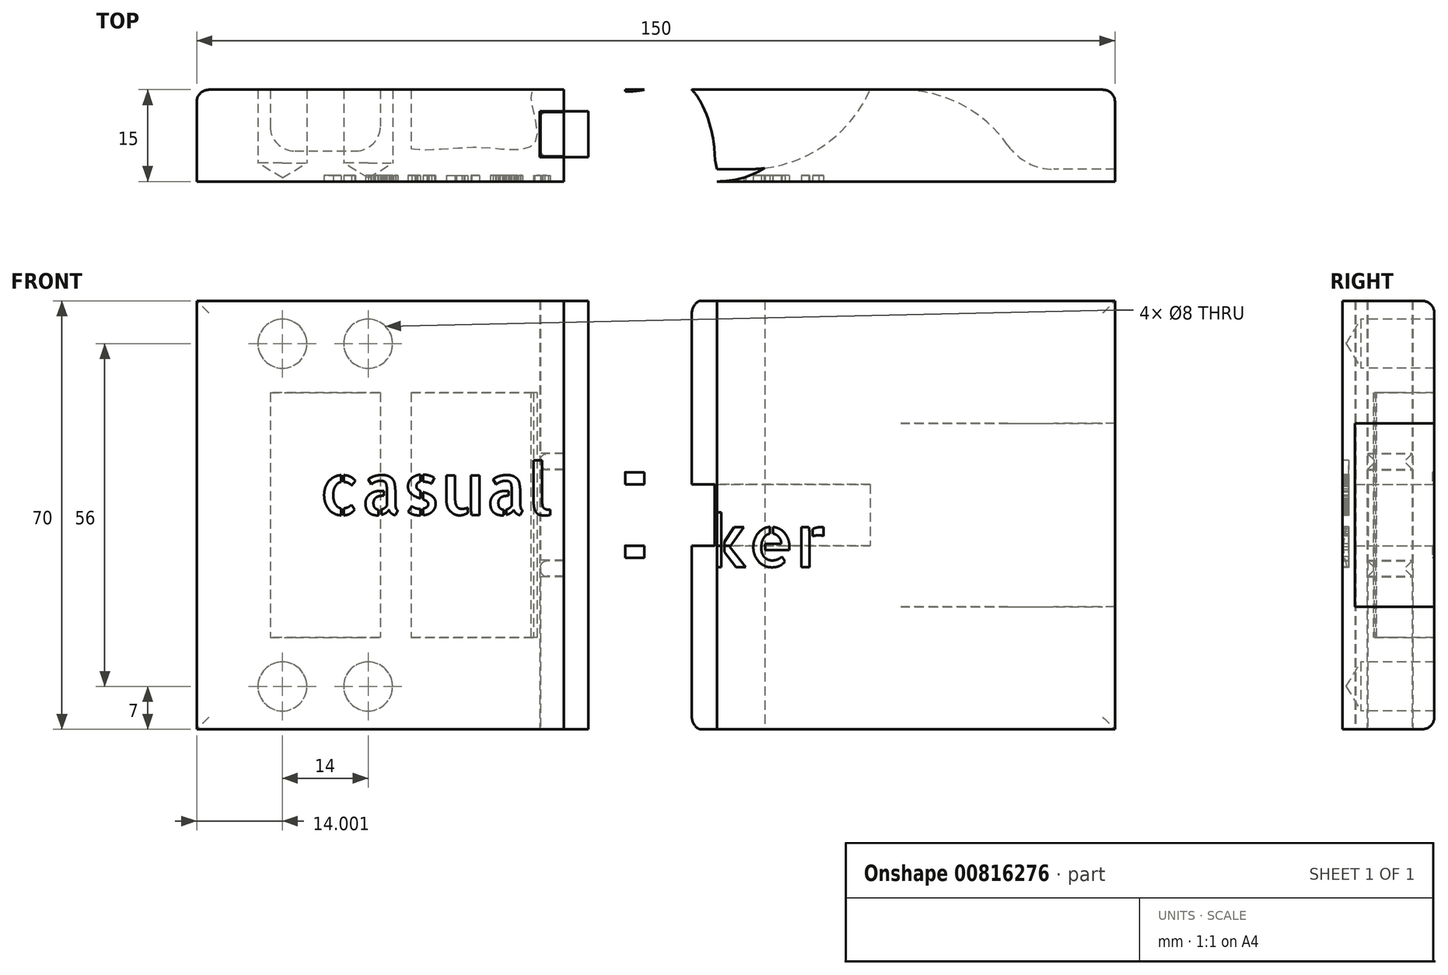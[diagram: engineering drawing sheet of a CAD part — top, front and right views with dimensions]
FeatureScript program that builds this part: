
annotation { "Feature Type Name" : "Feature", "Feature Type Description" : "" }
export const myFeature = defineFeature(function(context is Context, id is Id, definition is map)
    precondition{}
    {
        {
            var Q0;
            Q0=qCreatedBy(makeId("Top.planeOp"),FACE);
            var sketch = newSketch(context, id + "F0", { "sketchPlane" : qUnion([Q0])});
            skLineSegment(sketch, "E0.bottom", {"start": v(91.44, -7.74) * mm, "end": v(-58.56, -7.74) * mm});
            skLineSegment(sketch, "E0.top", {"start": v(91.44, 7.26) * mm, "end": v(-58.56, 7.26) * mm});
            skLineSegment(sketch, "E0.left", {"start": v(91.44, -7.74) * mm, "end": v(91.44, 7.26) * mm});
            skLineSegment(sketch, "E0.right", {"start": v(-58.56, -7.74) * mm, "end": v(-58.56, 7.26) * mm});
            skLineSegment(sketch, "E1", {"start": v(91.44, -5.74) * mm, "end": v(81.44, -5.74) * mm});
            skArc(sketch, "E2", {"start": v(81.44, -5.74) * mm, "mid": v(77.21, -4.7) * mm, "end": v(73.94, -1.84) * mm});
            skArc(sketch, "E3", {"start": v(73.94, -1.84) * mm, "mid": v(66.3, 4.85) * mm, "end": v(56.44, 7.26) * mm});
            skLineSegment(sketch, "E4", {"start": v(26.44, -5.74) * mm, "end": v(31.44, -5.74) * mm});
            skArc(sketch, "E5", {"start": v(31.44, -5.74) * mm, "mid": v(43.37, -2.2) * mm, "end": v(51.44, 7.26) * mm});
            skLineSegment(sketch, "E6", {"start": v(-58.56, -5.74) * mm, "end": v(106.76, -5.74) * mm, "construction": true});
            skFitSpline(sketch, "E7", {"points": [v(26.44, -5.74) * mm, v(25.26, -0.18) * mm, v(21.4, 5.71) * mm, v(6.44, 7.26) * mm], "startDerivative": vector(-4.01, 21.25) * mm, "endDerivative": vector(-55.89, 0) * mm});
            skLineSegment(sketch, "E8.bottom", {"start": v(-46.56, 7.26) * mm, "end": v(-28.56, 7.26) * mm});
            skLineSegment(sketch, "E8.top", {"start": v(-42.56, -2.74) * mm, "end": v(-32.56, -2.74) * mm});
            skLineSegment(sketch, "E8.left", {"start": v(-46.56, 7.26) * mm, "end": v(-46.56, 1.26) * mm});
            skLineSegment(sketch, "E8.right", {"start": v(-28.56, 7.26) * mm, "end": v(-28.56, 1.26) * mm});
            skLineSegment(sketch, "E9", {"start": v(-23.56, 7.26) * mm, "end": v(-23.56, -2.34) * mm});
            skFitSpline(sketch, "E10", {"points": [v(-23.56, -2.34) * mm, v(-16.77, -2.34) * mm, v(-10.45, -2.1) * mm, v(-4.83, 0) * mm, v(-3.56, 7.26) * mm], "startDerivative": vector(19.96, -2.18) * mm, "endDerivative": vector(3.98, 19.09) * mm});
            skPoint(sketch, "E11.visualSharp", {"position": v(-46.56, -2.74) * mm});
            skArc(sketch, "E11.filletArc", {"start": v(-46.56, 1.26) * mm, "mid": v(-45.39, -1.56) * mm, "end": v(-42.56, -2.74) * mm});
            skPoint(sketch, "E12.visualSharp", {"position": v(-28.56, -2.74) * mm});
            skArc(sketch, "E12.filletArc", {"start": v(-32.56, -2.74) * mm, "mid": v(-29.73, -1.56) * mm, "end": v(-28.56, 1.26) * mm});
            skCircle(sketch, "E13", {"center": v(26.44, 7.26) * mm, "radius": 15 * mm});
            skSolve(sketch);
        }
        {
            var Q0;
            Q0=qCreatedBy(makeId("Top.planeOp"),FACE);
            var sketch = newSketch(context, id + "F1", { "sketchPlane" : qUnion([Q0])});
            skFitSpline(sketch, "E14.0", {"points": [v(-23.56, -2.34) * mm, v(-21.87, -2.52) * mm, v(-16.45, -2.3) * mm, v(-10.78, -2.22) * mm, v(-3.3, -1.43) * mm, v(-3.9, 5.58) * mm, v(-3.56, 7.26) * mm]});
            skLineSegment(sketch, "E14.1", {"start": v(-23.56, 7.26) * mm, "end": v(-23.56, -2.34) * mm});
            skLineSegment(sketch, "E14.2", {"start": v(-28.56, 7.26) * mm, "end": v(-28.56, 1.26) * mm});
            skArc(sketch, "E14.3", {"start": v(-32.56, -2.74) * mm, "mid": v(-29.73, -1.56) * mm, "end": v(-28.56, 1.26) * mm});
            skLineSegment(sketch, "E14.4", {"start": v(-42.56, -2.74) * mm, "end": v(-32.56, -2.74) * mm});
            skArc(sketch, "E14.5", {"start": v(-46.56, 1.26) * mm, "mid": v(-45.39, -1.56) * mm, "end": v(-42.56, -2.74) * mm});
            skLineSegment(sketch, "E14.6", {"start": v(-46.56, 7.26) * mm, "end": v(-46.56, 1.26) * mm});
            skLineSegment(sketch, "E14.8", {"start": v(-58.56, -7.74) * mm, "end": v(-58.56, 7.26) * mm});
            skLineSegment(sketch, "E15", {"start": v(-58.56, -7.74) * mm, "end": v(1.44, -7.74) * mm});
            skLineSegment(sketch, "E16", {"start": v(1.44, -7.74) * mm, "end": v(1.44, 7.26) * mm});
            skLineSegment(sketch, "E17", {"start": v(1.44, 7.26) * mm, "end": v(-58.56, 7.26) * mm});
            skLineSegment(sketch, "E18.bottom", {"start": v(5.44, -3.75) * mm, "end": v(-2.56, -3.75) * mm});
            skLineSegment(sketch, "E18.top", {"start": v(5.44, 3.75) * mm, "end": v(-2.56, 3.75) * mm});
            skLineSegment(sketch, "E18.left", {"start": v(5.44, -3.75) * mm, "end": v(5.44, 3.75) * mm});
            skLineSegment(sketch, "E18.right", {"start": v(-2.56, -3.75) * mm, "end": v(-2.56, 3.75) * mm});
            skPoint(sketch, "E18.middle", {"position": v(1.44, 0) * mm});
            skFitSpline(sketch, "E19.0", {"points": [v(26.44, -5.74) * mm, v(26.08, -3.84) * mm, v(25.69, -0.2) * mm, v(21.45, 7.91) * mm, v(14.55, 7.26) * mm, v(6.44, 7.26) * mm]});
            skArc(sketch, "E19.1", {"start": v(31.44, -5.74) * mm, "mid": v(43.37, -2.2) * mm, "end": v(51.44, 7.26) * mm});
            skLineSegment(sketch, "E19.2", {"start": v(26.44, -5.74) * mm, "end": v(31.44, -5.74) * mm});
            skArc(sketch, "E19.3", {"start": v(73.94, -1.84) * mm, "mid": v(66.3, 4.85) * mm, "end": v(56.44, 7.26) * mm});
            skArc(sketch, "E19.4", {"start": v(81.44, -5.74) * mm, "mid": v(77.21, -4.7) * mm, "end": v(73.94, -1.84) * mm});
            skLineSegment(sketch, "E19.5", {"start": v(91.44, -5.74) * mm, "end": v(81.44, -5.74) * mm});
            skCircle(sketch, "E19.7", {"center": v(26.44, 7.26) * mm, "radius": 15 * mm});
            skLineSegment(sketch, "E20.bottom", {"start": v(1.44, 7.26) * mm, "end": v(91.44, 7.26) * mm});
            skLineSegment(sketch, "E20.top", {"start": v(1.44, -7.74) * mm, "end": v(91.44, -7.74) * mm});
            skLineSegment(sketch, "E20.left", {"start": v(1.44, 7.26) * mm, "end": v(1.44, -7.74) * mm});
            skLineSegment(sketch, "E20.right", {"start": v(91.44, 7.26) * mm, "end": v(91.44, -7.74) * mm});
            skLineSegment(sketch, "E21.0", {"start": v(8.94, 3.6) * mm, "end": v(-2.4, 3.6) * mm});
            skLineSegment(sketch, "E21.1", {"start": v(-2.4, -3.6) * mm, "end": v(-2.4, 3.6) * mm});
            skLineSegment(sketch, "E21.2", {"start": v(12.44, -3.6) * mm, "end": v(-2.4, -3.6) * mm});
            skSolve(sketch);
        }
        {
            var Q0;
            {var subQ5=sQuery(id+"F1.wireOp",EDGE,"E18.right");Q0=makeQuery(id+"F1.imprint","IMPRINT",FACE,{"disambiguationData":[TD([[makeQuery(id+"F1.imprint","IMPRINT",EDGE,{"derivedFrom":subQ5}),-1.0]])]});}
            var Q1;
            {var subQ6=sQuery(id+"F1.wireOp",EDGE,"E14.0");Q1=makeQuery(id+"F1.imprint","IMPRINT",FACE,{"disambiguationData":[TD([[makeQuery(id+"F1.imprint","IMPRINT",EDGE,{"derivedFrom":subQ6}),-1.0]])]});}
            var Q2;
            {var subQ0=sQuery(id+"F1.wireOp",EDGE,"E14.0");Q2=makeQuery(id+"F1.imprint","IMPRINT",FACE,{"disambiguationData":[TD([[makeQuery(id+"F1.imprint","IMPRINT",EDGE,{"derivedFrom":subQ0}),1.0]])]});}
            var Q3;
            {var subQ1=sQuery(id+"F1.wireOp",EDGE,"E14.2");Q3=makeQuery(id+"F1.imprint","IMPRINT",FACE,{"disambiguationData":[TD([[makeQuery(id+"F1.imprint","IMPRINT",EDGE,{"derivedFrom":subQ1}),-1.0]])]});}
            var Q4;
            {var subQ5=sQuery(id+"F1.wireOp",EDGE,"E21.1");Q4=makeQuery(id+"F1.imprint","IMPRINT",FACE,{"disambiguationData":[TD([[makeQuery(id+"F1.imprint","IMPRINT",EDGE,{"derivedFrom":subQ5}),-1.0]])]});}
            var Q5;
            {var subQ1=sQuery(id+"F1.wireOp",EDGE,"E14.1");Q5=makeQuery(id+"F1.imprint","IMPRINT",FACE,{"disambiguationData":[TD([[makeQuery(id+"F1.imprint","IMPRINT",EDGE,{"derivedFrom":subQ1}),-1.0]])]});}
            var Q6;
            {var subQ1=sQuery(id+"F1.wireOp",EDGE,"E21.1");var subQ3=sQuery(id+"F1.wireOp",EDGE,"E14.0");var subQ4=makeQuery(id+"F1.imprint","INTERSECT",VERTEX,{"derivedFrom":[subQ3,subQ1]});Q6=makeQuery(id+"F1.imprint","IMPRINT",FACE,{"disambiguationData":[TD([[makeQuery(id+"F1.imprint","IMPRINT",EDGE,{"disambiguationData":[TD([[subQ4,-1.0]])],"derivedFrom":subQ3}),-1.0]])]});}
            extrude(context, id + "F2", {"entities" : qUnion([Q0, Q1, Q2, Q3, Q4, Q5, Q6]), "depth" : 70 * mm, "offsetDistance" : 25 * mm, "symmetric" : true});
        }
        {
            var Q0;
            {var subQ1=sQuery(id+"F1.wireOp",EDGE,"E14.2");Q0=makeQuery(id+"F1.imprint","IMPRINT",FACE,{"disambiguationData":[TD([[makeQuery(id+"F1.imprint","IMPRINT",EDGE,{"derivedFrom":subQ1}),-1.0]])]});}
            var Q1;
            {var subQ0=sQuery(id+"F1.wireOp",EDGE,"E14.0");Q1=makeQuery(id+"F1.imprint","IMPRINT",FACE,{"disambiguationData":[TD([[makeQuery(id+"F1.imprint","IMPRINT",EDGE,{"derivedFrom":subQ0}),1.0]])]});}
            extrude(context, id + "F3", {"entities" : qUnion([Q0, Q1]), "operationType" : NewBodyOperationType.REMOVE, "depth" : 40 * mm, "offsetDistance" : 25 * mm, "symmetric" : true});
        }
        {
            var Q0;
            {var subQ5=sQuery(id+"F1.wireOp",EDGE,"E18.right");Q0=makeQuery(id+"F1.imprint","IMPRINT",FACE,{"disambiguationData":[TD([[makeQuery(id+"F1.imprint","IMPRINT",EDGE,{"derivedFrom":subQ5}),-1.0]])]});}
            var Q1;
            {var subQ5=sQuery(id+"F1.wireOp",EDGE,"E21.1");Q1=makeQuery(id+"F1.imprint","IMPRINT",FACE,{"disambiguationData":[TD([[makeQuery(id+"F1.imprint","IMPRINT",EDGE,{"derivedFrom":subQ5}),-1.0]])]});}
            extrude(context, id + "F4", {"entities" : qUnion([Q0, Q1]), "operationType" : NewBodyOperationType.REMOVE, "depth" : 20.25 * mm, "offsetDistance" : 25 * mm, "symmetric" : true});
        }
        {
            var Q0;
            {var subQ4=sQuery(id+"F1.wireOp",EDGE,"E18.left");Q0=makeQuery(id+"F1.imprint","IMPRINT",FACE,{"disambiguationData":[TD([[makeQuery(id+"F1.imprint","IMPRINT",EDGE,{"derivedFrom":subQ4}),-1.0]])]});}
            var Q1;
            {var subQ0=sQuery(id+"F1.wireOp",EDGE,"E18.left");Q1=makeQuery(id+"F1.imprint","IMPRINT",FACE,{"disambiguationData":[TD([[makeQuery(id+"F1.imprint","IMPRINT",EDGE,{"derivedFrom":subQ0}),1.0]])]});}
            var Q2;
            {var subQ4=sQuery(id+"F1.wireOp",EDGE,"E19.3");Q2=makeQuery(id+"F1.imprint","IMPRINT",FACE,{"disambiguationData":[TD([[makeQuery(id+"F1.imprint","IMPRINT",EDGE,{"derivedFrom":subQ4}),1.0]])]});}
            var Q3;
            {var subQ1=sQuery(id+"F1.wireOp",EDGE,"E19.3");Q3=makeQuery(id+"F1.imprint","IMPRINT",FACE,{"disambiguationData":[TD([[makeQuery(id+"F1.imprint","IMPRINT",EDGE,{"derivedFrom":subQ1}),-1.0]])]});}
            var Q4;
            {var subQ0=sQuery(id+"F1.wireOp",EDGE,"E20.bottom");var subQ1=sQuery(id+"F1.wireOp",EDGE,"E19.1");var subQ2=makeQuery(id+"F1.imprint","INTERSECT",VERTEX,{"derivedFrom":[subQ1,subQ0]});Q4=makeQuery(id+"F1.imprint","IMPRINT",FACE,{"disambiguationData":[TD([[makeQuery(id+"F1.imprint","IMPRINT",EDGE,{"disambiguationData":[TD([[subQ2,1.0]])],"derivedFrom":subQ1}),1.0]])]});}
            var Q5;
            {var subQ4=sQuery(id+"F1.wireOp",EDGE,"E19.2");Q5=makeQuery(id+"F1.imprint","IMPRINT",FACE,{"disambiguationData":[TD([[makeQuery(id+"F1.imprint","IMPRINT",EDGE,{"derivedFrom":subQ4}),-1.0]])]});}
            var Q6;
            {var subQ5=sQuery(id+"F1.wireOp",EDGE,"E19.2");Q6=makeQuery(id+"F1.imprint","IMPRINT",FACE,{"disambiguationData":[TD([[makeQuery(id+"F1.imprint","IMPRINT",EDGE,{"derivedFrom":subQ5}),1.0]])]});}
            extrude(context, id + "F5", {"entities" : qUnion([Q0, Q1, Q2, Q3, Q4, Q5, Q6]), "depth" : 70 * mm, "offsetDistance" : 25 * mm, "symmetric" : true});
        }
        {
            var Q0;
            {var subQ0=sQuery(id+"F1.wireOp",EDGE,"E19.7");var subQ1=sQuery(id+"F1.wireOp",EDGE,"E19.0");var subQ2=makeQuery(id+"F1.imprint","INTERSECT",VERTEX,{"derivedFrom":[subQ1,subQ0]});Q0=makeQuery(id+"F1.imprint","IMPRINT",FACE,{"disambiguationData":[TD([[makeQuery(id+"F1.imprint","IMPRINT",EDGE,{"disambiguationData":[TD([[subQ2,1.0]])],"derivedFrom":subQ1}),-1.0]])]});}
            extrude(context, id + "F6", {"entities" : qUnion([Q0]), "operationType" : NewBodyOperationType.ADD, "depth" : 14 * mm, "offsetDistance" : 25 * mm, "symmetric" : true});
        }
        {
            var Q0;
            {var subQ0=sQuery(id+"F1.wireOp",EDGE,"E19.7");var subQ1=sQuery(id+"F1.wireOp",EDGE,"E19.0");var subQ2=makeQuery(id+"F1.imprint","INTERSECT",VERTEX,{"disambiguationData":[OD(0.0)],"derivedFrom":[subQ1,subQ0]});Q0=makeQuery(id+"F1.imprint","IMPRINT",FACE,{"disambiguationData":[TD([[makeQuery(id+"F1.imprint","IMPRINT",EDGE,{"disambiguationData":[TD([[subQ2,1.0]])],"derivedFrom":subQ1}),-1.0]])]});}
            var Q1;
            {var subQ1=sQuery(id+"F0.wireOp",EDGE,"E4");Q1=makeQuery(id+"F0.imprint","IMPRINT",FACE,{"disambiguationData":[TD([[makeQuery(id+"F0.imprint","IMPRINT",EDGE,{"derivedFrom":subQ1}),1.0]])]});}
            var Q2;
            {var subQ0=sQuery(id+"F0.wireOp",EDGE,"E5");var subQ1=sQuery(id+"F0.wireOp",EDGE,"E0.top");var subQ2=makeQuery(id+"F0.imprint","INTERSECT",VERTEX,{"derivedFrom":[subQ1,subQ0]});Q2=makeQuery(id+"F0.imprint","IMPRINT",FACE,{"disambiguationData":[TD([[makeQuery(id+"F0.imprint","IMPRINT",EDGE,{"disambiguationData":[TD([[subQ2,-1.0]])],"derivedFrom":subQ1}),1.0]])]});}
            extrude(context, id + "F7", {"entities" : qUnion([Q0, Q1, Q2]), "operationType" : NewBodyOperationType.REMOVE, "depth" : 10 * mm, "offsetDistance" : 25 * mm, "symmetric" : true});
        }
        {
            var Q0;
            {var subQ0=sQuery(id+"F1.wireOp",EDGE,"E19.7");var subQ1=sQuery(id+"F1.wireOp",EDGE,"E19.0");var subQ2=makeQuery(id+"F1.imprint","INTERSECT",VERTEX,{"disambiguationData":[OD(1.0)],"derivedFrom":[subQ1,subQ0]});Q0=makeQuery(id+"F1.imprint","IMPRINT",FACE,{"disambiguationData":[TD([[makeQuery(id+"F1.imprint","IMPRINT",EDGE,{"disambiguationData":[TD([[subQ2,-1.0]])],"derivedFrom":subQ1}),-1.0]])]});}
            var Q1;
            {var subQ5=sQuery(id+"F1.wireOp",EDGE,"E19.1");Q1=makeQuery(id+"F1.imprint","IMPRINT",FACE,{"disambiguationData":[TD([[makeQuery(id+"F1.imprint","IMPRINT",EDGE,{"derivedFrom":subQ5}),1.0]])]});}
            extrude(context, id + "F8", {"entities" : qUnion([Q0, Q1]), "operationType" : NewBodyOperationType.REMOVE, "oppositeDirection" : true, "depth" : 10 * mm, "offsetDistance" : 25 * mm, "symmetric" : true});
        }
        {
            var Q0;
            {var subQ1=sQuery(id+"F1.wireOp",EDGE,"E19.3");Q0=makeQuery(id+"F1.imprint","IMPRINT",FACE,{"disambiguationData":[TD([[makeQuery(id+"F1.imprint","IMPRINT",EDGE,{"derivedFrom":subQ1}),-1.0]])]});}
            extrude(context, id + "F9", {"entities" : qUnion([Q0]), "operationType" : NewBodyOperationType.REMOVE, "depth" : 30 * mm, "offsetDistance" : 25 * mm, "symmetric" : true});
        }
        {
            var Q0;
            {var subQ5=sQuery(id+"F1.wireOp",EDGE,"E21.1");Q0=makeQuery(id+"F1.imprint","IMPRINT",FACE,{"disambiguationData":[TD([[makeQuery(id+"F1.imprint","IMPRINT",EDGE,{"derivedFrom":subQ5}),-1.0]])]});}
            extrude(context, id + "F10", {"entities" : qUnion([Q0]), "operationType" : NewBodyOperationType.ADD, "depth" : 20 * mm, "offsetDistance" : 25 * mm, "symmetric" : true});
        }
        {
            var Q0;
            {var subQ0=sQuery(id+"F1.wireOp",EDGE,"E20.bottom");var subQ1=makeQuery(id+"F1.imprint","INTERSECT",VERTEX,{"derivedFrom":[sQuery(id+"F1.wireOp",EDGE,"E19.3"),subQ0]});var subQ2=makeQuery(id+"F1.imprint","INTERSECT",VERTEX,{"derivedFrom":[sQuery(id+"F1.wireOp",EDGE,"E19.1"),subQ0]});var subQ3=sQuery(id+"F1.wireOp",EDGE,"E19.7");var subQ4=makeQuery(id+"F1.imprint","INTERSECT",VERTEX,{"disambiguationData":[OD(0.0)],"derivedFrom":[subQ3,subQ0]});var subQ5=sQuery(id+"F1.wireOp",EDGE,"E19.0");var subQ6=makeQuery(id+"F1.imprint","INTERSECT",VERTEX,{"disambiguationData":[OD(1.0)],"derivedFrom":[subQ5,subQ0]});var subQ8=makeQuery(id+"F1.imprint","INTERSECT",VERTEX,{"disambiguationData":[OD(0.0)],"derivedFrom":[subQ5,subQ0]});Q0=makeQuery(id+"Fk8vee3glepebii_2.boolean.opBoolean","MERGE",EDGE,{"derivedFrom":[makeQuery(id+"F5.opExtrude","CAP_EDGE",EDGE,{"disambiguationData":[OSD([subQ0]),TDD([makeQuery(id+"F1.imprint","IMPRINT",EDGE,{"disambiguationData":[TD([[subQ8,1.0]])],"derivedFrom":subQ0}),makeQuery(id+"F1.imprint","IMPRINT",EDGE,{"disambiguationData":[TD([[subQ8,-1.0]])],"derivedFrom":subQ0})])],"isStart":false}),makeQuery(id+"F5.opExtrude","CAP_EDGE",EDGE,{"disambiguationData":[OSD([subQ0]),TDD([makeQuery(id+"F1.imprint","IMPRINT",EDGE,{"disambiguationData":[TD([[subQ2,-1.0]])],"derivedFrom":subQ0})])],"isStart":false}),makeQuery(id+"Fk8vee3glepebii_2.opExtrude","CAP_EDGE",EDGE,{"disambiguationData":[OSD([subQ0]),TDD([makeQuery(id+"F1.imprint","IMPRINT",EDGE,{"disambiguationData":[TD([[subQ6,1.0]])],"derivedFrom":subQ0}),makeQuery(id+"F1.imprint","IMPRINT",EDGE,{"disambiguationData":[TD([[subQ4,1.0]])],"derivedFrom":subQ0}),makeQuery(id+"F1.imprint","IMPRINT",EDGE,{"disambiguationData":[TD([[subQ2,1.0]])],"derivedFrom":subQ0})])],"isStart":false}),makeQuery(id+"Fk8vee3glepebii_2.opExtrude","CAP_EDGE",EDGE,{"disambiguationData":[OSD([subQ0]),TDD([makeQuery(id+"F1.imprint","IMPRINT",EDGE,{"disambiguationData":[TD([[subQ1,-1.0]])],"derivedFrom":subQ0})])],"isStart":false})]});}
            var Q1;
            {var subQ0=sQuery(id+"F1.wireOp",EDGE,"E20.bottom");var subQ3=sQuery(id+"F1.wireOp",EDGE,"E20.right");var subQ4=sQuery(id+"F1.wireOp",EDGE,"E19.1");var subQ6=sQuery(id+"F1.wireOp",EDGE,"E19.7");var subQ8=sQuery(id+"F1.wireOp",EDGE,"E19.0");var subQ13=sQuery(id+"F1.wireOp",EDGE,"E19.2");Q1=makeQuery(id+"F9.boolean.opBoolean","SPLIT",EDGE,{"disambiguationData":[TD([makeQuery(id+"Fk8vee3glepebii_2.opExtrude","CAP_FACE",FACE,{"disambiguationData":[OSD([subQ8,subQ4,subQ13,subQ6,subQ0])],"isStart":false})])],"derivedFrom":makeQuery(id+"Fk8vee3glepebii_2.opExtrude","SWEPT_EDGE",EDGE,{"disambiguationData":[OSD([subQ0,subQ3])]})});}
            var Q2;
            {var subQ0=sQuery(id+"F1.wireOp",EDGE,"E20.right");var subQ1=sQuery(id+"F1.wireOp",EDGE,"E20.bottom");var subQ2=sQuery(id+"F1.wireOp",EDGE,"E19.1");var subQ4=sQuery(id+"F1.wireOp",EDGE,"E19.7");var subQ6=sQuery(id+"F1.wireOp",EDGE,"E19.0");var subQ11=sQuery(id+"F1.wireOp",EDGE,"E19.2");Q2=makeQuery(id+"F9.boolean.opBoolean","SPLIT",EDGE,{"disambiguationData":[TD([makeQuery(id+"Fk8vee3glepebii_2.opExtrude","CAP_FACE",FACE,{"disambiguationData":[OSD([subQ6,subQ2,subQ11,subQ4,subQ1])],"isStart":true})])],"derivedFrom":makeQuery(id+"Fk8vee3glepebii_2.opExtrude","SWEPT_EDGE",EDGE,{"disambiguationData":[OSD([subQ1,subQ0])]})});}
            var Q3;
            {var subQ0=sQuery(id+"F1.wireOp",EDGE,"E20.bottom");var subQ1=makeQuery(id+"F1.imprint","INTERSECT",VERTEX,{"derivedFrom":[sQuery(id+"F1.wireOp",EDGE,"E19.3"),subQ0]});var subQ2=makeQuery(id+"F1.imprint","INTERSECT",VERTEX,{"derivedFrom":[sQuery(id+"F1.wireOp",EDGE,"E19.1"),subQ0]});var subQ3=sQuery(id+"F1.wireOp",EDGE,"E19.7");var subQ4=makeQuery(id+"F1.imprint","INTERSECT",VERTEX,{"disambiguationData":[OD(0.0)],"derivedFrom":[subQ3,subQ0]});var subQ5=sQuery(id+"F1.wireOp",EDGE,"E19.0");var subQ6=makeQuery(id+"F1.imprint","INTERSECT",VERTEX,{"disambiguationData":[OD(1.0)],"derivedFrom":[subQ5,subQ0]});var subQ8=makeQuery(id+"F1.imprint","INTERSECT",VERTEX,{"disambiguationData":[OD(0.0)],"derivedFrom":[subQ5,subQ0]});Q3=makeQuery(id+"Fk8vee3glepebii_2.boolean.opBoolean","MERGE",EDGE,{"derivedFrom":[makeQuery(id+"F5.opExtrude","CAP_EDGE",EDGE,{"disambiguationData":[OSD([subQ0]),TDD([makeQuery(id+"F1.imprint","IMPRINT",EDGE,{"disambiguationData":[TD([[subQ8,1.0]])],"derivedFrom":subQ0}),makeQuery(id+"F1.imprint","IMPRINT",EDGE,{"disambiguationData":[TD([[subQ8,-1.0]])],"derivedFrom":subQ0})])],"isStart":true}),makeQuery(id+"F5.opExtrude","CAP_EDGE",EDGE,{"disambiguationData":[OSD([subQ0]),TDD([makeQuery(id+"F1.imprint","IMPRINT",EDGE,{"disambiguationData":[TD([[subQ2,-1.0]])],"derivedFrom":subQ0})])],"isStart":true}),makeQuery(id+"Fk8vee3glepebii_2.opExtrude","CAP_EDGE",EDGE,{"disambiguationData":[OSD([subQ0]),TDD([makeQuery(id+"F1.imprint","IMPRINT",EDGE,{"disambiguationData":[TD([[subQ6,1.0]])],"derivedFrom":subQ0}),makeQuery(id+"F1.imprint","IMPRINT",EDGE,{"disambiguationData":[TD([[subQ4,1.0]])],"derivedFrom":subQ0}),makeQuery(id+"F1.imprint","IMPRINT",EDGE,{"disambiguationData":[TD([[subQ2,1.0]])],"derivedFrom":subQ0})])],"isStart":true}),makeQuery(id+"Fk8vee3glepebii_2.opExtrude","CAP_EDGE",EDGE,{"disambiguationData":[OSD([subQ0]),TDD([makeQuery(id+"F1.imprint","IMPRINT",EDGE,{"disambiguationData":[TD([[subQ1,-1.0]])],"derivedFrom":subQ0})])],"isStart":true})]});}
            var Q4;
            Q4=makeQuery(id+"F2.opExtrude","CAP_EDGE",EDGE,{"disambiguationData":[OSD([sQuery(id+"F1.wireOp",EDGE,"E17")])],"isStart":false});
            var Q5;
            Q5=makeQuery(id+"F2.opExtrude","SWEPT_EDGE",EDGE,{"disambiguationData":[OSD([sQuery(id+"F1.wireOp",EDGE,"E14.8"),sQuery(id+"F1.wireOp",EDGE,"E17")])]});
            var Q6;
            Q6=makeQuery(id+"F2.opExtrude","CAP_EDGE",EDGE,{"disambiguationData":[OSD([sQuery(id+"F1.wireOp",EDGE,"E17")])],"isStart":true});
            var Q7;
            Q7=makeQuery(id+"F3.boolean.opBoolean","COPY",EDGE,{"derivedFrom":makeQuery(id+"F3.opExtrude","SWEPT_EDGE",EDGE,{"disambiguationData":[OSD([sQuery(id+"F1.wireOp",EDGE,"E14.6"),sQuery(id+"F1.wireOp",EDGE,"E17")])]})});
            var Q8;
            Q8=makeQuery(id+"F3.boolean.opBoolean","COPY",EDGE,{"derivedFrom":makeQuery(id+"F3.opExtrude","SWEPT_EDGE",EDGE,{"disambiguationData":[OSD([sQuery(id+"F1.wireOp",EDGE,"E14.2"),sQuery(id+"F1.wireOp",EDGE,"E17")])]})});
            var Q9;
            Q9=makeQuery(id+"F3.boolean.opBoolean","COPY",EDGE,{"derivedFrom":makeQuery(id+"F3.opExtrude","SWEPT_EDGE",EDGE,{"disambiguationData":[OSD([sQuery(id+"F1.wireOp",EDGE,"E14.1"),sQuery(id+"F1.wireOp",EDGE,"E17")])]})});
            var Q10;
            {var subQ0=sQuery(id+"F1.wireOp",EDGE,"E17");Q10=makeQuery(id+"F3.boolean.opBoolean","COPY",EDGE,{"derivedFrom":makeQuery(id+"F3.opExtrude","CAP_EDGE",EDGE,{"disambiguationData":[OSD([subQ0]),TDD([makeQuery(id+"F1.imprint","IMPRINT",EDGE,{"disambiguationData":[TD([[makeQuery(id+"F1.imprint","INTERSECT",VERTEX,{"derivedFrom":[sQuery(id+"F1.wireOp",EDGE,"E14.2"),subQ0]}),-1.0]])],"derivedFrom":subQ0})])],"isStart":true})});}
            var Q11;
            {var subQ0=sQuery(id+"F1.wireOp",EDGE,"E17");Q11=makeQuery(id+"F3.boolean.opBoolean","COPY",EDGE,{"derivedFrom":makeQuery(id+"F3.opExtrude","CAP_EDGE",EDGE,{"disambiguationData":[OSD([subQ0]),TDD([makeQuery(id+"F1.imprint","IMPRINT",EDGE,{"disambiguationData":[TD([[makeQuery(id+"F1.imprint","INTERSECT",VERTEX,{"derivedFrom":[sQuery(id+"F1.wireOp",EDGE,"E14.2"),subQ0]}),-1.0]])],"derivedFrom":subQ0})])],"isStart":false})});}
            var Q12;
            {var subQ0=sQuery(id+"F1.wireOp",EDGE,"E20.bottom");var subQ1=sQuery(id+"F1.wireOp",EDGE,"E20.right");Q12=makeQuery(id+"F9.boolean.opBoolean","SPLIT",EDGE,{"disambiguationData":[TD([makeQuery(id+"F5.opExtrude","CAP_FACE",FACE,{"disambiguationData":[OSD([subQ0,sQuery(id+"F1.wireOp",EDGE,"E20.top"),sQuery(id+"F1.wireOp",EDGE,"E20.left"),subQ1])],"isStart":false})])],"derivedFrom":makeQuery(id+"F5.opExtrude","SWEPT_EDGE",EDGE,{"disambiguationData":[OSD([subQ0,subQ1])]})});}
            var Q13;
            {var subQ0=sQuery(id+"F1.wireOp",EDGE,"E20.bottom");var subQ1=sQuery(id+"F1.wireOp",EDGE,"E20.right");Q13=makeQuery(id+"F9.boolean.opBoolean","SPLIT",EDGE,{"disambiguationData":[TD([makeQuery(id+"F5.opExtrude","CAP_FACE",FACE,{"disambiguationData":[OSD([subQ0,sQuery(id+"F1.wireOp",EDGE,"E20.top"),sQuery(id+"F1.wireOp",EDGE,"E20.left"),subQ1])],"isStart":true})])],"derivedFrom":makeQuery(id+"F5.opExtrude","SWEPT_EDGE",EDGE,{"disambiguationData":[OSD([subQ0,subQ1])]})});}
            fillet(context, id + "F11", {"entities" : qUnion([Q0, Q1, Q2, Q3, Q4, Q5, Q6, Q7, Q8, Q9, Q10, Q11, Q12, Q13]), "radius" : 2 * mm, "tangentPropagation" : true, "allowEdgeOverflow" : false});
        }
        {
            var Q0;
            {var subQ5=sQuery(id+"F1.wireOp",EDGE,"E21.1");Q0=makeQuery(id+"F1.imprint","IMPRINT",FACE,{"disambiguationData":[TD([[makeQuery(id+"F1.imprint","IMPRINT",EDGE,{"derivedFrom":subQ5}),-1.0]])]});}
            extrude(context, id + "F12", {"entities" : qUnion([Q0]), "operationType" : NewBodyOperationType.REMOVE, "depth" : 15 * mm, "offsetDistance" : 25 * mm, "symmetric" : true});
        }
        {
            var Q0;
            {var subQ0=sQuery(id+"F1.wireOp",EDGE,"E21.2");var subQ1=sQuery(id+"F1.wireOp",EDGE,"E21.1");var subQ2=sQuery(id+"F1.wireOp",EDGE,"E21.0");var subQ3=sQuery(id+"F1.wireOp",EDGE,"E20.left");Q0=makeQuery(id+"F12.boolean.opBoolean","SPLIT",FACE,{"disambiguationData":[TD([makeQuery(id+"F10.opExtrude","CAP_FACE",FACE,{"disambiguationData":[OSD([subQ3,subQ2,subQ1,subQ0])],"isStart":true})])],"derivedFrom":makeQuery(id+"F10.opExtrude","SWEPT_FACE",FACE,{"disambiguationData":[OSD([subQ1])]})});}
            var Q1;
            {var subQ0=sQuery(id+"F1.wireOp",EDGE,"E21.2");var subQ1=sQuery(id+"F1.wireOp",EDGE,"E21.1");var subQ2=sQuery(id+"F1.wireOp",EDGE,"E21.0");var subQ3=sQuery(id+"F1.wireOp",EDGE,"E20.left");Q1=makeQuery(id+"F12.boolean.opBoolean","SPLIT",FACE,{"disambiguationData":[TD([makeQuery(id+"F10.opExtrude","CAP_FACE",FACE,{"disambiguationData":[OSD([subQ3,subQ2,subQ1,subQ0])],"isStart":false})])],"derivedFrom":makeQuery(id+"F10.opExtrude","SWEPT_FACE",FACE,{"disambiguationData":[OSD([subQ1])]})});}
            fillet(context, id + "F13", {"entities" : qUnion([Q0, Q1]), "radius" : 1 * mm, "tangentPropagation" : true, "allowEdgeOverflow" : false});
        }
        {
            var Q0;
            {var subQ5=sQuery(id+"F1.wireOp",EDGE,"E21.1");Q0=makeQuery(id+"F1.imprint","IMPRINT",FACE,{"disambiguationData":[TD([[makeQuery(id+"F1.imprint","IMPRINT",EDGE,{"derivedFrom":subQ5}),-1.0]])]});}
            var Q1;
            {var subQ5=sQuery(id+"F1.wireOp",EDGE,"E18.right");Q1=makeQuery(id+"F1.imprint","IMPRINT",FACE,{"disambiguationData":[TD([[makeQuery(id+"F1.imprint","IMPRINT",EDGE,{"derivedFrom":subQ5}),-1.0]])]});}
            extrude(context, id + "F14", {"entities" : qUnion([Q0, Q1]), "operationType" : NewBodyOperationType.ADD, "depth" : 14.75 * mm, "offsetDistance" : 25 * mm, "symmetric" : true});
        }
        {
            var Q0;
            Q0=makeQuery(id+"F2.opExtrude","SWEPT_FACE",FACE,{"disambiguationData":[OSD([sQuery(id+"F1.wireOp",EDGE,"E15")])]});
            var sketch = newSketch(context, id + "F15", { "sketchPlane" : qUnion([Q0])});
            skText(sketch, "E22", { "text": "casual", "fontName": "AllertaStencil-Regular.ttf"});
            skText(sketch, "E23", { "text": "Tanker", "fontName": "AllertaStencil-Regular.ttf"});
            const initialGuessF15  = {"E22": [-0.03855, 0, 1, 0, 0.0085], "E23": [0.00288, -0.0085, 1, 0, 0.0085]};
            skSetInitialGuess(sketch, initialGuessF15);
            skSolve(sketch);
        }
        {
            var Q0;
            Q0=makeQuery(id+"F15.imprint","IMPRINT",FACE,{"disambiguationData":[TD([[makeQuery(id+"F15.imprint","IMPRINT",EDGE,{"derivedFrom":sQuery(id+"F15.wireOp",EDGE,"E22.sketch_text.stroke-11")}),-1.0]])]});
            var Q1;
            Q1=makeQuery(id+"F15.imprint","IMPRINT",FACE,{"disambiguationData":[TD([[makeQuery(id+"F15.imprint","IMPRINT",EDGE,{"derivedFrom":sQuery(id+"F15.wireOp",EDGE,"E22.sketch_text.stroke-0")}),-1.0]])]});
            var Q2;
            Q2=makeQuery(id+"F15.imprint","IMPRINT",FACE,{"disambiguationData":[TD([[makeQuery(id+"F15.imprint","IMPRINT",EDGE,{"derivedFrom":sQuery(id+"F15.wireOp",EDGE,"E22.sketch_text.stroke-5")}),-1.0]])]});
            var Q3;
            Q3=makeQuery(id+"F15.imprint","IMPRINT",FACE,{"disambiguationData":[TD([[makeQuery(id+"F15.imprint","IMPRINT",EDGE,{"derivedFrom":sQuery(id+"F15.wireOp",EDGE,"E22.sketch_text.stroke-29")}),-1.0]])]});
            var Q4;
            Q4=makeQuery(id+"F15.imprint","IMPRINT",FACE,{"disambiguationData":[TD([[makeQuery(id+"F15.imprint","IMPRINT",EDGE,{"derivedFrom":sQuery(id+"F15.wireOp",EDGE,"E22.sketch_text.stroke-48")}),-1.0]])]});
            var Q5;
            Q5=makeQuery(id+"F15.imprint","IMPRINT",FACE,{"disambiguationData":[TD([[makeQuery(id+"F15.imprint","IMPRINT",EDGE,{"derivedFrom":sQuery(id+"F15.wireOp",EDGE,"E22.sketch_text.stroke-84")}),-1.0]])]});
            var Q6;
            Q6=makeQuery(id+"F15.imprint","IMPRINT",FACE,{"disambiguationData":[TD([[makeQuery(id+"F15.imprint","IMPRINT",EDGE,{"derivedFrom":sQuery(id+"F15.wireOp",EDGE,"E22.sketch_text.stroke-98")}),-1.0]])]});
            var Q7;
            Q7=makeQuery(id+"F15.imprint","IMPRINT",FACE,{"disambiguationData":[TD([[makeQuery(id+"F15.imprint","IMPRINT",EDGE,{"derivedFrom":sQuery(id+"F15.wireOp",EDGE,"E22.sketch_text.stroke-113")}),-1.0]])]});
            var Q8;
            Q8=makeQuery(id+"F15.imprint","IMPRINT",FACE,{"disambiguationData":[TD([[makeQuery(id+"F15.imprint","IMPRINT",EDGE,{"derivedFrom":sQuery(id+"F15.wireOp",EDGE,"E22.sketch_text.stroke-104")}),-1.0]])]});
            var Q9;
            Q9=makeQuery(id+"F15.imprint","IMPRINT",FACE,{"disambiguationData":[TD([[makeQuery(id+"F15.imprint","IMPRINT",EDGE,{"derivedFrom":sQuery(id+"F15.wireOp",EDGE,"E22.sketch_text.stroke-127")}),-1.0]])]});
            var Q10;
            Q10=makeQuery(id+"F15.imprint","IMPRINT",FACE,{"disambiguationData":[TD([[makeQuery(id+"F15.imprint","IMPRINT",EDGE,{"derivedFrom":sQuery(id+"F15.wireOp",EDGE,"E22.sketch_text.stroke-147")}),-1.0]])]});
            var Q11;
            Q11=makeQuery(id+"F15.imprint","IMPRINT",FACE,{"disambiguationData":[TD([[makeQuery(id+"F15.imprint","IMPRINT",EDGE,{"derivedFrom":sQuery(id+"F15.wireOp",EDGE,"E22.sketch_text.stroke-152")}),-1.0]])]});
            var Q12;
            Q12=makeQuery(id+"F15.imprint","IMPRINT",FACE,{"disambiguationData":[TD([[makeQuery(id+"F15.imprint","IMPRINT",EDGE,{"derivedFrom":sQuery(id+"F15.wireOp",EDGE,"E22.sketch_text.stroke-171")}),-1.0]])]});
            var Q13;
            Q13=makeQuery(id+"F15.imprint","IMPRINT",FACE,{"disambiguationData":[TD([[makeQuery(id+"F15.imprint","IMPRINT",EDGE,{"derivedFrom":sQuery(id+"F15.wireOp",EDGE,"E22.sketch_text.stroke-207")}),-1.0]])]});
            var Q14;
            Q14=makeQuery(id+"F15.imprint","IMPRINT",FACE,{"disambiguationData":[TD([[makeQuery(id+"F15.imprint","IMPRINT",EDGE,{"derivedFrom":sQuery(id+"F15.wireOp",EDGE,"E22.sketch_text.stroke-12")}),-1.0]])]});
            extrude(context, id + "F16", {"entities" : qUnion([Q0, Q1, Q2, Q3, Q4, Q5, Q6, Q7, Q8, Q9, Q10, Q11, Q12, Q13, Q14]), "operationType" : NewBodyOperationType.REMOVE, "oppositeDirection" : true, "depth" : 1 * mm, "offsetDistance" : 25 * mm});
        }
        {
            var Q0;
            Q0=makeQuery(id+"F15.imprint","IMPRINT",FACE,{"disambiguationData":[TD([[makeQuery(id+"F15.imprint","IMPRINT",EDGE,{"derivedFrom":sQuery(id+"F15.wireOp",EDGE,"E23.sketch_text.stroke-0")}),-1.0]])]});
            var Q1;
            Q1=makeQuery(id+"F15.imprint","IMPRINT",FACE,{"disambiguationData":[TD([[makeQuery(id+"F15.imprint","IMPRINT",EDGE,{"derivedFrom":sQuery(id+"F15.wireOp",EDGE,"E23.sketch_text.stroke-8")}),-1.0]])]});
            var Q2;
            Q2=makeQuery(id+"F15.imprint","IMPRINT",FACE,{"disambiguationData":[TD([[makeQuery(id+"F15.imprint","IMPRINT",EDGE,{"derivedFrom":sQuery(id+"F15.wireOp",EDGE,"E23.sketch_text.stroke-27")}),-1.0]])]});
            var Q3;
            Q3=makeQuery(id+"F15.imprint","IMPRINT",FACE,{"disambiguationData":[TD([[makeQuery(id+"F15.imprint","IMPRINT",EDGE,{"derivedFrom":sQuery(id+"F15.wireOp",EDGE,"E23.sketch_text.stroke-63")}),-1.0]])]});
            var Q4;
            Q4=makeQuery(id+"F15.imprint","IMPRINT",FACE,{"disambiguationData":[TD([[makeQuery(id+"F15.imprint","IMPRINT",EDGE,{"derivedFrom":sQuery(id+"F15.wireOp",EDGE,"E23.sketch_text.stroke-68")}),-1.0]])]});
            var Q5;
            Q5=makeQuery(id+"F15.imprint","IMPRINT",FACE,{"disambiguationData":[TD([[makeQuery(id+"F15.imprint","IMPRINT",EDGE,{"derivedFrom":sQuery(id+"F15.wireOp",EDGE,"E23.sketch_text.stroke-94")}),-1.0]])]});
            var Q6;
            Q6=makeQuery(id+"F15.imprint","IMPRINT",FACE,{"disambiguationData":[TD([[makeQuery(id+"F15.imprint","IMPRINT",EDGE,{"derivedFrom":sQuery(id+"F15.wireOp",EDGE,"E23.sketch_text.stroke-87")}),-1.0]])]});
            var Q7;
            Q7=makeQuery(id+"F15.imprint","IMPRINT",FACE,{"disambiguationData":[TD([[makeQuery(id+"F15.imprint","IMPRINT",EDGE,{"derivedFrom":sQuery(id+"F15.wireOp",EDGE,"E23.sketch_text.stroke-111")}),-1.0]])]});
            var Q8;
            Q8=makeQuery(id+"F15.imprint","IMPRINT",FACE,{"disambiguationData":[TD([[makeQuery(id+"F15.imprint","IMPRINT",EDGE,{"derivedFrom":sQuery(id+"F15.wireOp",EDGE,"E23.sketch_text.stroke-98")}),-1.0]])]});
            var Q9;
            Q9=makeQuery(id+"F15.imprint","IMPRINT",FACE,{"disambiguationData":[TD([[makeQuery(id+"F15.imprint","IMPRINT",EDGE,{"derivedFrom":sQuery(id+"F15.wireOp",EDGE,"E23.sketch_text.stroke-135")}),-1.0]])]});
            var Q10;
            Q10=makeQuery(id+"F15.imprint","IMPRINT",FACE,{"disambiguationData":[TD([[makeQuery(id+"F15.imprint","IMPRINT",EDGE,{"derivedFrom":sQuery(id+"F15.wireOp",EDGE,"E23.sketch_text.stroke-142")}),-1.0]])]});
            extrude(context, id + "F17", {"entities" : qUnion([Q0, Q1, Q2, Q3, Q4, Q5, Q6, Q7, Q8, Q9, Q10]), "operationType" : NewBodyOperationType.REMOVE, "oppositeDirection" : true, "depth" : 1 * mm, "offsetDistance" : 25 * mm});
        }
        {
            var Q0;
            Q0=makeQuery(id+"F2.opExtrude","SWEPT_FACE",FACE,{"disambiguationData":[OSD([sQuery(id+"F1.wireOp",EDGE,"E17")])]});
            var sketch = newSketch(context, id + "F18", { "sketchPlane" : qUnion([Q0])});
            skPoint(sketch, "E24.MirrorP", {"position": v(37.6, 0.24) * mm});
            skPoint(sketch, "E25", {"position": v(44.56, -28) * mm});
            skPoint(sketch, "E26", {"position": v(30.56, -28) * mm});
            skPoint(sketch, "E27.MirrorP", {"position": v(30.56, 28) * mm});
            skPoint(sketch, "E28.MirrorP", {"position": v(44.56, 28) * mm});
            skSolve(sketch);
        }
        {
            var Q0;
            Q0=sQuery(id+"F18.wireOp",VERTEX,"E25");
            var Q1;
            Q1=sQuery(id+"F18.wireOp",VERTEX,"E26");
            var Q2;
            Q2=sQuery(id+"F18.wireOp",VERTEX,"E28.MirrorP");
            var Q3;
            Q3=sQuery(id+"F18.wireOp",VERTEX,"E27.MirrorP");
            var Q4;
            Q4=makeQuery(id+"F2.opExtrude","SWEPT_BODY",BODY,{"disambiguationData":[OSD([sQuery(id+"F1.wireOp",EDGE,"E14.8"),sQuery(id+"F1.wireOp",EDGE,"E15"),sQuery(id+"F1.wireOp",EDGE,"E17"),sQuery(id+"F1.wireOp",EDGE,"E20.left")])]});
            hole(context, id + "F19", {"style" : HoleStyle.SIMPLE, "endStyle" : HoleEndStyle.BLIND, "holeDiameter" : 8 * mm, "majorDiameter" : 5 * mm, "holeDepth" : 12 * mm, "isTappedThrough" : true, "tappedDepth" : 12 * mm, "tapClearance" : 3, "locations" : qUnion([Q0, Q1, Q2, Q3]), "scope" : qUnion([Q4]), "startStyle" : HoleStartStyle.PART});
        }
    });
